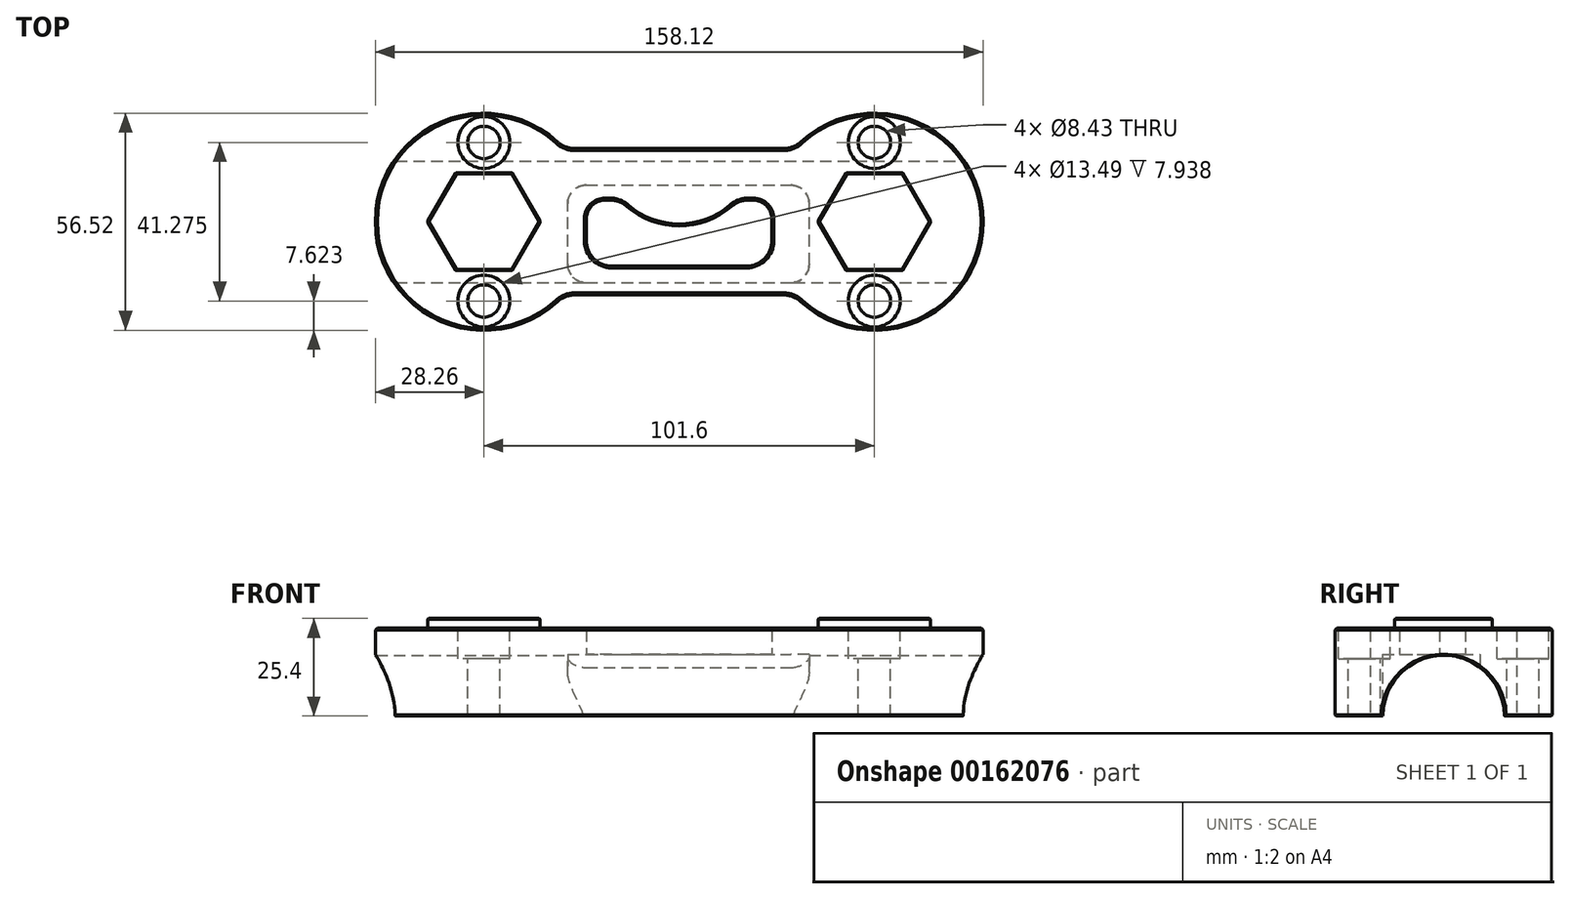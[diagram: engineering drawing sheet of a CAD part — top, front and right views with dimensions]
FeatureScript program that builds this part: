
annotation { "Feature Type Name" : "Feature", "Feature Type Description" : "" }
export const myFeature = defineFeature(function(context is Context, id is Id, definition is map)
    precondition{}
    {
        {
            var Q0;
            Q0=qCreatedBy(makeId("Top.planeOp"),FACE);
            var sketch = newSketch(context, id + "F0", { "sketchPlane" : qUnion([Q0])});
            skPoint(sketch, "E0", {"position": v(-50.8, 0) * mm});
            skPoint(sketch, "E1", {"position": v(50.8, 0) * mm});
            skArc(sketch, "E2", {"start": v(-31.67, 20.8) * mm, "mid": v(-79.06, 0) * mm, "end": v(-31.67, -20.8) * mm});
            skArc(sketch, "E3", {"start": v(31.67, -20.8) * mm, "mid": v(79.06, 0) * mm, "end": v(31.67, 20.8) * mm});
            skLineSegment(sketch, "E4", {"start": v(-27.2, 19.05) * mm, "end": v(27.2, 19.05) * mm});
            skLineSegment(sketch, "E5", {"start": v(-27.2, -19.05) * mm, "end": v(27.2, -19.05) * mm});
            skPoint(sketch, "E6.orphan", {"position": v(-45.55, -19.05) * mm});
            skPoint(sketch, "E7.orphan", {"position": v(-45.55, 19.05) * mm});
            skPoint(sketch, "E8.orphan", {"position": v(44.18, 19.05) * mm});
            skPoint(sketch, "E9.orphan", {"position": v(44.18, -19.05) * mm});
            skPoint(sketch, "E10.visualSharp", {"position": v(-29.93, 19.05) * mm});
            skArc(sketch, "E10.filletArc", {"start": v(-31.67, 20.8) * mm, "mid": v(-29.6, 19.5) * mm, "end": v(-27.2, 19.05) * mm});
            skPoint(sketch, "E11.visualSharp", {"position": v(29.93, 19.05) * mm});
            skArc(sketch, "E11.filletArc", {"start": v(27.2, 19.05) * mm, "mid": v(29.6, 19.5) * mm, "end": v(31.67, 20.8) * mm});
            skPoint(sketch, "E12.visualSharp", {"position": v(-29.93, -19.05) * mm});
            skArc(sketch, "E12.filletArc", {"start": v(-27.2, -19.05) * mm, "mid": v(-29.6, -19.5) * mm, "end": v(-31.67, -20.8) * mm});
            skPoint(sketch, "E13.visualSharp", {"position": v(29.93, -19.05) * mm});
            skArc(sketch, "E13.filletArc", {"start": v(31.67, -20.8) * mm, "mid": v(29.6, -19.5) * mm, "end": v(27.2, -19.05) * mm});
            skSolve(sketch);
        }
        {
            var Q0;
            Q0=qSketchRegion(id+"F0",true);
            extrude(context, id + "F1", {"entities" : qUnion([Q0]), "depth" : 22.86 * mm});
        }
        {
            var Q0;
            Q0=qCreatedBy(makeId("Right.planeOp"),FACE);
            var sketch = newSketch(context, id + "F2", { "sketchPlane" : qUnion([Q0])});
            skCircle(sketch, "E14", {"center": v(0, 0) * mm, "radius": 15.81 * mm});
            skSolve(sketch);
        }
        {
            var Q0;
            Q0=qSketchRegion(id+"F2",true);
            extrude(context, id + "F3", {"entities" : qUnion([Q0]), "operationType" : NewBodyOperationType.REMOVE, "endBound" : BoundingType.THROUGH_ALL, "oppositeDirection" : true, "depth" : 25.4 * mm, "hasSecondDirection" : true, "secondDirectionBound" : SecondDirectionBoundingType.THROUGH_ALL, "secondDirectionOppositeDirection" : false, "secondDirectionDepth" : 25.4 * mm});
        }
        {
            var Q0;
            Q0=qCreatedBy(makeId("Top.planeOp"),FACE);
            var sketch = newSketch(context, id + "F4", { "sketchPlane" : qUnion([Q0])});
            skPoint(sketch, "E15", {"position": v(-50.73, 0.06) * mm});
            skPoint(sketch, "E16", {"position": v(50.87, 0.06) * mm});
            skLineSegment(sketch, "E17.bottom", {"start": v(-24.18, -15.88) * mm, "end": v(29.02, -15.87) * mm});
            skLineSegment(sketch, "E17.top", {"start": v(-24.18, 9.52) * mm, "end": v(29.02, 9.53) * mm});
            skLineSegment(sketch, "E17.left", {"start": v(-29, -11.05) * mm, "end": v(-29, 4.7) * mm});
            skLineSegment(sketch, "E17.right", {"start": v(33.84, -11.05) * mm, "end": v(33.84, 4.7) * mm});
            skPoint(sketch, "E18.visualSharp", {"position": v(-29, -15.88) * mm});
            skArc(sketch, "E18.filletArc", {"start": v(-29, -11.05) * mm, "mid": v(-27.6, -14.46) * mm, "end": v(-24.18, -15.88) * mm});
            skPoint(sketch, "E19.visualSharp", {"position": v(-29, 9.52) * mm});
            skArc(sketch, "E19.filletArc", {"start": v(-24.18, 9.52) * mm, "mid": v(-27.6, 8.11) * mm, "end": v(-29, 4.7) * mm});
            skPoint(sketch, "E20.visualSharp", {"position": v(33.84, 9.53) * mm});
            skArc(sketch, "E20.filletArc", {"start": v(33.84, 4.7) * mm, "mid": v(32.43, 8.11) * mm, "end": v(29.02, 9.52) * mm});
            skPoint(sketch, "E21.visualSharp", {"position": v(33.84, -15.87) * mm});
            skArc(sketch, "E21.filletArc", {"start": v(29.02, -15.87) * mm, "mid": v(32.43, -14.46) * mm, "end": v(33.84, -11.05) * mm});
            skSolve(sketch);
        }
        {
            var Q0;
            Q0=qSketchRegion(id+"F4",true);
            extrude(context, id + "F5", {"entities" : qUnion([Q0]), "operationType" : NewBodyOperationType.REMOVE, "depth" : 16 * mm});
        }
        {
            var Q0;
            Q0=makeQuery(id+"F5.boolean.opBoolean","COPY",FACE,{"derivedFrom":makeQuery(id+"F5.opExtrude","CAP_FACE",FACE,{"disambiguationData":[OSD([sQuery(id+"F4.wireOp",EDGE,"E17.bottom"),sQuery(id+"F4.wireOp",EDGE,"E17.top"),sQuery(id+"F4.wireOp",EDGE,"E17.left"),sQuery(id+"F4.wireOp",EDGE,"E17.right")])],"isStart":false})});
            var sketch = newSketch(context, id + "F6", { "sketchPlane" : qUnion([Q0])});
            skPoint(sketch, "E22.middle", {"position": v(0, 0) * mm});
            skLineSegment(sketch, "E23.bottom", {"start": v(-17.53, 11.52) * mm, "end": v(17.53, 11.52) * mm});
            skLineSegment(sketch, "E23.top", {"start": v(-19.3, -5.63) * mm, "end": v(-17.92, -5.63) * mm});
            skLineSegment(sketch, "E23.left", {"start": v(-24.13, 4.91) * mm, "end": v(-24.13, -0.8) * mm});
            skLineSegment(sketch, "E23.right", {"start": v(24.13, 4.91) * mm, "end": v(24.13, -0.8) * mm});
            skPoint(sketch, "E23.middle", {"position": v(0, 2.94) * mm});
            skPoint(sketch, "E24", {"position": v(-15.24, -5.63) * mm});
            skPoint(sketch, "E25", {"position": v(15.24, -5.63) * mm});
            skArc(sketch, "E26", {"start": v(13.57, -4) * mm, "mid": v(0, 1.1) * mm, "end": v(-13.57, -4) * mm});
            skLineSegment(sketch, "E27.trimOffspring", {"start": v(17.92, -5.63) * mm, "end": v(19.3, -5.63) * mm});
            skPoint(sketch, "E28.visualSharp", {"position": v(-24.13, 11.52) * mm});
            skArc(sketch, "E28.filletArc", {"start": v(-17.53, 11.52) * mm, "mid": v(-22.2, 9.58) * mm, "end": v(-24.13, 4.91) * mm});
            skPoint(sketch, "E29.visualSharp", {"position": v(24.13, 11.52) * mm});
            skArc(sketch, "E29.filletArc", {"start": v(24.13, 4.91) * mm, "mid": v(22.2, 9.58) * mm, "end": v(17.53, 11.52) * mm});
            skPoint(sketch, "E30.visualSharp", {"position": v(-24.13, -5.63) * mm});
            skArc(sketch, "E30.filletArc", {"start": v(-24.13, -0.8) * mm, "mid": v(-22.72, -4.21) * mm, "end": v(-19.3, -5.63) * mm});
            skArc(sketch, "E31.filletArc", {"start": v(-17.92, -5.63) * mm, "mid": v(-15.6, -5.2) * mm, "end": v(-13.57, -4) * mm});
            skPoint(sketch, "E32.visualSharp", {"position": v(24.13, -5.63) * mm});
            skArc(sketch, "E32.filletArc", {"start": v(19.3, -5.63) * mm, "mid": v(22.72, -4.21) * mm, "end": v(24.13, -0.8) * mm});
            skArc(sketch, "E33.filletArc", {"start": v(13.57, -4) * mm, "mid": v(15.6, -5.2) * mm, "end": v(17.92, -5.63) * mm});
            skSolve(sketch);
        }
        {
            var Q0;
            Q0=qSketchRegion(id+"F6",true);
            extrude(context, id + "F7", {"entities" : qUnion([Q0]), "operationType" : NewBodyOperationType.REMOVE, "oppositeDirection" : true, "depth" : 25.4 * mm});
        }
        {
            var Q0;
            Q0=makeQuery(id+"F1.opExtrude","CAP_FACE",FACE,{"disambiguationData":[OSD([sQuery(id+"F0.wireOp",EDGE,"E2"),sQuery(id+"F0.wireOp",EDGE,"E3"),sQuery(id+"F0.wireOp",EDGE,"E4"),sQuery(id+"F0.wireOp",EDGE,"E5"),sQuery(id+"F0.wireOp",EDGE,"E10.filletArc"),sQuery(id+"F0.wireOp",EDGE,"E11.filletArc"),sQuery(id+"F0.wireOp",EDGE,"E12.filletArc"),sQuery(id+"F0.wireOp",EDGE,"E13.filletArc")])],"isStart":false});
            var sketch = newSketch(context, id + "F8", { "sketchPlane" : qUnion([Q0])});
            skCircle(sketch, "E34", {"center": v(-50.8, 0) * mm, "radius": 12.7 * mm});
            skCircle(sketch, "E35", {"center": v(50.8, 0) * mm, "radius": 12.7 * mm});
            skCircle(sketch, "E36.cCircle", {"center": v(-50.8, 0) * mm, "radius": 12.7 * mm, "construction": true});
            skLineSegment(sketch, "E36.0", {"start": v(-58.13, 12.7) * mm, "end": v(-43.47, 12.7) * mm});
            skLineSegment(sketch, "E36.1", {"start": v(-43.47, 12.7) * mm, "end": v(-36.14, 0) * mm});
            skLineSegment(sketch, "E36.2", {"start": v(-36.14, 0) * mm, "end": v(-43.47, -12.7) * mm});
            skLineSegment(sketch, "E36.3", {"start": v(-43.47, -12.7) * mm, "end": v(-58.13, -12.7) * mm});
            skLineSegment(sketch, "E36.4", {"start": v(-58.13, -12.7) * mm, "end": v(-65.46, 0) * mm});
            skLineSegment(sketch, "E36.5", {"start": v(-65.46, 0) * mm, "end": v(-58.13, 12.7) * mm});
            skPoint(sketch, "E36.0.midPoint", {"position": v(-50.8, 12.7) * mm});
            skCircle(sketch, "E37.cCircle", {"center": v(50.8, 0) * mm, "radius": 12.7 * mm, "construction": true});
            skLineSegment(sketch, "E37.0", {"start": v(43.47, 12.7) * mm, "end": v(58.13, 12.7) * mm});
            skLineSegment(sketch, "E37.1", {"start": v(58.13, 12.7) * mm, "end": v(65.46, 0) * mm});
            skLineSegment(sketch, "E37.2", {"start": v(65.46, 0) * mm, "end": v(58.13, -12.7) * mm});
            skLineSegment(sketch, "E37.3", {"start": v(58.13, -12.7) * mm, "end": v(43.47, -12.7) * mm});
            skLineSegment(sketch, "E37.4", {"start": v(43.47, -12.7) * mm, "end": v(36.14, 0) * mm});
            skLineSegment(sketch, "E37.5", {"start": v(36.14, 0) * mm, "end": v(43.47, 12.7) * mm});
            skPoint(sketch, "E37.0.midPoint", {"position": v(50.8, 12.7) * mm});
            skSolve(sketch);
        }
        {
            var Q0;
            Q0=qSketchRegion(id+"F8",true);
            extrude(context, id + "F9", {"entities" : qUnion([Q0]), "operationType" : NewBodyOperationType.ADD, "depth" : 2.54 * mm});
        }
        {
            var Q0;
            Q0=makeQuery(id+"F1.opExtrude","CAP_FACE",FACE,{"disambiguationData":[OSD([sQuery(id+"F0.wireOp",EDGE,"E2"),sQuery(id+"F0.wireOp",EDGE,"E3"),sQuery(id+"F0.wireOp",EDGE,"E4"),sQuery(id+"F0.wireOp",EDGE,"E5"),sQuery(id+"F0.wireOp",EDGE,"E10.filletArc"),sQuery(id+"F0.wireOp",EDGE,"E11.filletArc"),sQuery(id+"F0.wireOp",EDGE,"E12.filletArc"),sQuery(id+"F0.wireOp",EDGE,"E13.filletArc")])],"isStart":false});
            var sketch = newSketch(context, id + "F10", { "sketchPlane" : qUnion([Q0])});
            skPoint(sketch, "E38.startSnap0", {"position": v(-50.8, 12.7) * mm});
            skPoint(sketch, "E39.startSnap0", {"position": v(50.8, 12.7) * mm});
            skPoint(sketch, "E39.endSnap0", {"position": v(50.8, -12.7) * mm});
            skPoint(sketch, "E40", {"position": v(-50.8, 20.64) * mm});
            skPoint(sketch, "E41", {"position": v(-50.8, -20.64) * mm});
            skPoint(sketch, "E42", {"position": v(50.8, 20.64) * mm});
            skPoint(sketch, "E43", {"position": v(50.8, -20.64) * mm});
            skSolve(sketch);
        }
        {
            var Q0;
            Q0=sQuery(id+"F10.wireOp",VERTEX,"E40");
            var Q1;
            Q1=sQuery(id+"F10.wireOp",VERTEX,"E41");
            var Q2;
            Q2=sQuery(id+"F10.wireOp",VERTEX,"E42");
            var Q3;
            Q3=sQuery(id+"F10.wireOp",VERTEX,"E43");
            var Q4;
            Q4=makeQuery(id+"F1.opExtrude","SWEPT_BODY",BODY,{"disambiguationData":[OSD([sQuery(id+"F0.wireOp",EDGE,"E2"),sQuery(id+"F0.wireOp",EDGE,"E3"),sQuery(id+"F0.wireOp",EDGE,"E4"),sQuery(id+"F0.wireOp",EDGE,"E5"),sQuery(id+"F0.wireOp",EDGE,"E10.filletArc"),sQuery(id+"F0.wireOp",EDGE,"E11.filletArc"),sQuery(id+"F0.wireOp",EDGE,"E12.filletArc"),sQuery(id+"F0.wireOp",EDGE,"E13.filletArc")])]});
            hole(context, id + "F11", {"style" : HoleStyle.C_BORE, "endStyle" : HoleEndStyle.THROUGH, "standardTappedOrClearance" : lookupTablePath({ "standard" : "ANSI", "fit" : "Normal (ASME)", "size" : "5/16", "type" : "Clearance" }), "standardBlindInLast" : lookupTablePath({ "fit" : "Free", "standard" : "ANSI", "size" : "5/16", "type" : "Clearance" }), "holeDiameter" : 8.43 * mm, "cBoreDiameter" : 13.5 * mm, "cBoreDepth" : 7.94 * mm, "locations" : qUnion([Q0, Q1, Q2, Q3]), "scope" : qUnion([Q4]), "isTappedThrough" : true});
        }
        {
            var Q0;
            Q0=makeQuery(id+"F11.hole-0.boolean.opBoolean","COPY",EDGE,{"derivedFrom":makeQuery(id+"F11.hole-0.opRevolve","SWEPT_EDGE",EDGE,{"disambiguationData":[OSD([sQuery(id+"F11.hole-0.sketch.wireOp",EDGE,"cbore_start_line_2"),sQuery(id+"F11.hole-0.sketch.wireOp",EDGE,"cbore_start_line_3")])]})});
            var Q1;
            Q1=makeQuery(id+"F11.hole-1.boolean.opBoolean","COPY",EDGE,{"derivedFrom":makeQuery(id+"F11.hole-1.opRevolve","SWEPT_EDGE",EDGE,{"disambiguationData":[OSD([sQuery(id+"F11.hole-1.sketch.wireOp",EDGE,"cbore_start_line_2"),sQuery(id+"F11.hole-1.sketch.wireOp",EDGE,"cbore_start_line_3")])]})});
            var Q2;
            Q2=makeQuery(id+"F11.hole-3.boolean.opBoolean","COPY",EDGE,{"derivedFrom":makeQuery(id+"F11.hole-3.opRevolve","SWEPT_EDGE",EDGE,{"disambiguationData":[OSD([sQuery(id+"F11.hole-3.sketch.wireOp",EDGE,"cbore_start_line_2"),sQuery(id+"F11.hole-3.sketch.wireOp",EDGE,"cbore_start_line_3")])]})});
            var Q3;
            Q3=makeQuery(id+"F11.hole-2.boolean.opBoolean","COPY",EDGE,{"derivedFrom":makeQuery(id+"F11.hole-2.opRevolve","SWEPT_EDGE",EDGE,{"disambiguationData":[OSD([sQuery(id+"F11.hole-2.sketch.wireOp",EDGE,"cbore_start_line_2"),sQuery(id+"F11.hole-2.sketch.wireOp",EDGE,"cbore_start_line_3")])]})});
            var Q4;
            Q4=makeQuery(id+"F9.opExtrude","CAP_FACE",FACE,{"disambiguationData":[OSD([sQuery(id+"F8.wireOp",EDGE,"E36.0"),sQuery(id+"F8.wireOp",EDGE,"E36.1"),sQuery(id+"F8.wireOp",EDGE,"E36.2"),sQuery(id+"F8.wireOp",EDGE,"E36.3"),sQuery(id+"F8.wireOp",EDGE,"E36.4"),sQuery(id+"F8.wireOp",EDGE,"E36.5")])],"isStart":false});
            var Q5;
            Q5=makeQuery(id+"F9.opExtrude","CAP_FACE",FACE,{"disambiguationData":[OSD([sQuery(id+"F8.wireOp",EDGE,"E37.0"),sQuery(id+"F8.wireOp",EDGE,"E37.1"),sQuery(id+"F8.wireOp",EDGE,"E37.2"),sQuery(id+"F8.wireOp",EDGE,"E37.3"),sQuery(id+"F8.wireOp",EDGE,"E37.4"),sQuery(id+"F8.wireOp",EDGE,"E37.5")])],"isStart":false});
            chamfer(context, id + "F12", {"entities" : qUnion([Q0, Q1, Q2, Q3, Q4, Q5]), "width" : 0.25 * mm, "tangentPropagation" : true});
        }
        {
            var Q0;
            Q0=makeQuery(id+"F1.opExtrude","CAP_EDGE",EDGE,{"disambiguationData":[OSD([sQuery(id+"F0.wireOp",EDGE,"E12.filletArc")])],"isStart":false});
            var Q1;
            Q1=makeQuery(id+"F1.opExtrude","CAP_EDGE",EDGE,{"disambiguationData":[OSD([sQuery(id+"F0.wireOp",EDGE,"E2")])],"isStart":false});
            var Q2;
            Q2=makeQuery(id+"F7.boolean.opBoolean","INTERSECT",EDGE,{"derivedFrom":[makeQuery(id+"F1.opExtrude","CAP_FACE",FACE,{"disambiguationData":[OSD([sQuery(id+"F0.wireOp",EDGE,"E2"),sQuery(id+"F0.wireOp",EDGE,"E3"),sQuery(id+"F0.wireOp",EDGE,"E4"),sQuery(id+"F0.wireOp",EDGE,"E5"),sQuery(id+"F0.wireOp",EDGE,"E10.filletArc"),sQuery(id+"F0.wireOp",EDGE,"E11.filletArc"),sQuery(id+"F0.wireOp",EDGE,"E12.filletArc"),sQuery(id+"F0.wireOp",EDGE,"E13.filletArc")])],"isStart":false}),makeQuery(id+"F7.opExtrude","SWEPT_FACE",FACE,{"disambiguationData":[OSD([sQuery(id+"F6.wireOp",EDGE,"E23.left")])]})]});
            var Q3;
            Q3=makeQuery(id+"F7.boolean.opBoolean","INTERSECT",EDGE,{"derivedFrom":[makeQuery(id+"F1.opExtrude","CAP_FACE",FACE,{"disambiguationData":[OSD([sQuery(id+"F0.wireOp",EDGE,"E2"),sQuery(id+"F0.wireOp",EDGE,"E3"),sQuery(id+"F0.wireOp",EDGE,"E4"),sQuery(id+"F0.wireOp",EDGE,"E5"),sQuery(id+"F0.wireOp",EDGE,"E10.filletArc"),sQuery(id+"F0.wireOp",EDGE,"E11.filletArc"),sQuery(id+"F0.wireOp",EDGE,"E12.filletArc"),sQuery(id+"F0.wireOp",EDGE,"E13.filletArc")])],"isStart":false}),makeQuery(id+"F7.opExtrude","SWEPT_FACE",FACE,{"disambiguationData":[OSD([sQuery(id+"F6.wireOp",EDGE,"E30.filletArc")])]})]});
            chamfer(context, id + "F13", {"entities" : qUnion([Q0, Q1, Q2, Q3]), "width" : 0.5 * mm, "tangentPropagation" : true});
        }
        {
            var Q0;
            Q0=makeQuery(id+"F9.opExtrude","SWEPT_EDGE",EDGE,{"disambiguationData":[OSD([sQuery(id+"F8.wireOp",EDGE,"E36.2"),sQuery(id+"F8.wireOp",EDGE,"E36.3")])]});
            var Q1;
            Q1=makeQuery(id+"F9.opExtrude","SWEPT_EDGE",EDGE,{"disambiguationData":[OSD([sQuery(id+"F8.wireOp",EDGE,"E36.1"),sQuery(id+"F8.wireOp",EDGE,"E36.2")])]});
            var Q2;
            Q2=makeQuery(id+"F9.opExtrude","SWEPT_EDGE",EDGE,{"disambiguationData":[OSD([sQuery(id+"F8.wireOp",EDGE,"E36.3"),sQuery(id+"F8.wireOp",EDGE,"E36.4")])]});
            var Q3;
            Q3=makeQuery(id+"F9.opExtrude","SWEPT_EDGE",EDGE,{"disambiguationData":[OSD([sQuery(id+"F8.wireOp",EDGE,"E36.4"),sQuery(id+"F8.wireOp",EDGE,"E36.5")])]});
            var Q4;
            Q4=makeQuery(id+"F9.opExtrude","SWEPT_EDGE",EDGE,{"disambiguationData":[OSD([sQuery(id+"F8.wireOp",EDGE,"E36.0"),sQuery(id+"F8.wireOp",EDGE,"E36.5")])]});
            var Q5;
            Q5=makeQuery(id+"F9.opExtrude","SWEPT_EDGE",EDGE,{"disambiguationData":[OSD([sQuery(id+"F8.wireOp",EDGE,"E36.0"),sQuery(id+"F8.wireOp",EDGE,"E36.1")])]});
            var Q6;
            Q6=makeQuery(id+"F9.opExtrude","SWEPT_EDGE",EDGE,{"disambiguationData":[OSD([sQuery(id+"F8.wireOp",EDGE,"E37.2"),sQuery(id+"F8.wireOp",EDGE,"E37.3")])]});
            var Q7;
            Q7=makeQuery(id+"F9.opExtrude","SWEPT_EDGE",EDGE,{"disambiguationData":[OSD([sQuery(id+"F8.wireOp",EDGE,"E37.1"),sQuery(id+"F8.wireOp",EDGE,"E37.2")])]});
            var Q8;
            Q8=makeQuery(id+"F9.opExtrude","SWEPT_EDGE",EDGE,{"disambiguationData":[OSD([sQuery(id+"F8.wireOp",EDGE,"E37.3"),sQuery(id+"F8.wireOp",EDGE,"E37.4")])]});
            var Q9;
            Q9=makeQuery(id+"F9.opExtrude","SWEPT_EDGE",EDGE,{"disambiguationData":[OSD([sQuery(id+"F8.wireOp",EDGE,"E37.0"),sQuery(id+"F8.wireOp",EDGE,"E37.1")])]});
            var Q10;
            Q10=makeQuery(id+"F9.opExtrude","SWEPT_EDGE",EDGE,{"disambiguationData":[OSD([sQuery(id+"F8.wireOp",EDGE,"E37.0"),sQuery(id+"F8.wireOp",EDGE,"E37.5")])]});
            var Q11;
            Q11=makeQuery(id+"F9.opExtrude","SWEPT_EDGE",EDGE,{"disambiguationData":[OSD([sQuery(id+"F8.wireOp",EDGE,"E37.4"),sQuery(id+"F8.wireOp",EDGE,"E37.5")])]});
            fillet(context, id + "F14", {"entities" : qUnion([Q0, Q1, Q2, Q3, Q4, Q5, Q6, Q7, Q8, Q9, Q10, Q11]), "radius" : 0.25 * mm, "tangentPropagation" : true, "allowEdgeOverflow" : false});
        }
        {
            var Q0;
            {var subQ0=sQuery(id+"F0.wireOp",EDGE,"E2");var subQ1=sQuery(id+"F0.wireOp",EDGE,"E10.filletArc");Q0=makeQuery(id+"F3.boolean.opBoolean","SPLIT",EDGE,{"disambiguationData":[TD([makeQuery(id+"F1.opExtrude","SWEPT_FACE",FACE,{"disambiguationData":[OSD([subQ1])]})])],"derivedFrom":makeQuery(id+"F1.opExtrude","CAP_EDGE",EDGE,{"disambiguationData":[OSD([subQ0])],"isStart":true})});}
            var Q1;
            Q1=makeQuery(id+"F1.opExtrude","CAP_EDGE",EDGE,{"disambiguationData":[OSD([sQuery(id+"F0.wireOp",EDGE,"E10.filletArc")])],"isStart":true});
            var Q2;
            {var subQ0=sQuery(id+"F0.wireOp",EDGE,"E13.filletArc");var subQ1=sQuery(id+"F0.wireOp",EDGE,"E3");Q2=makeQuery(id+"F3.boolean.opBoolean","SPLIT",EDGE,{"disambiguationData":[TD([makeQuery(id+"F1.opExtrude","SWEPT_FACE",FACE,{"disambiguationData":[OSD([subQ0])]})])],"derivedFrom":makeQuery(id+"F1.opExtrude","CAP_EDGE",EDGE,{"disambiguationData":[OSD([subQ1])],"isStart":true})});}
            chamfer(context, id + "F15", {"entities" : qUnion([Q0, Q1, Q2]), "width" : 0.25 * mm, "tangentPropagation" : true});
        }
        {
            var Q0;
            Q0=makeQuery(id+"F3.boolean.opBoolean","INTERSECT",EDGE,{"derivedFrom":[makeQuery(id+"F1.opExtrude","SWEPT_FACE",FACE,{"disambiguationData":[OSD([sQuery(id+"F0.wireOp",EDGE,"E3")])]}),makeQuery(id+"F3.opExtrude","SWEPT_FACE",FACE,{"disambiguationData":[OSD([sQuery(id+"F2.wireOp",EDGE,"E14")])]})]});
            var Q1;
            Q1=makeQuery(id+"F3.boolean.opBoolean","INTERSECT",EDGE,{"derivedFrom":[makeQuery(id+"F1.opExtrude","SWEPT_FACE",FACE,{"disambiguationData":[OSD([sQuery(id+"F0.wireOp",EDGE,"E2")])]}),makeQuery(id+"F3.opExtrude","SWEPT_FACE",FACE,{"disambiguationData":[OSD([sQuery(id+"F2.wireOp",EDGE,"E14")])]})]});
            chamfer(context, id + "F16", {"entities" : qUnion([Q0, Q1]), "width" : 0.25 * mm, "tangentPropagation" : true});
        }
    });
